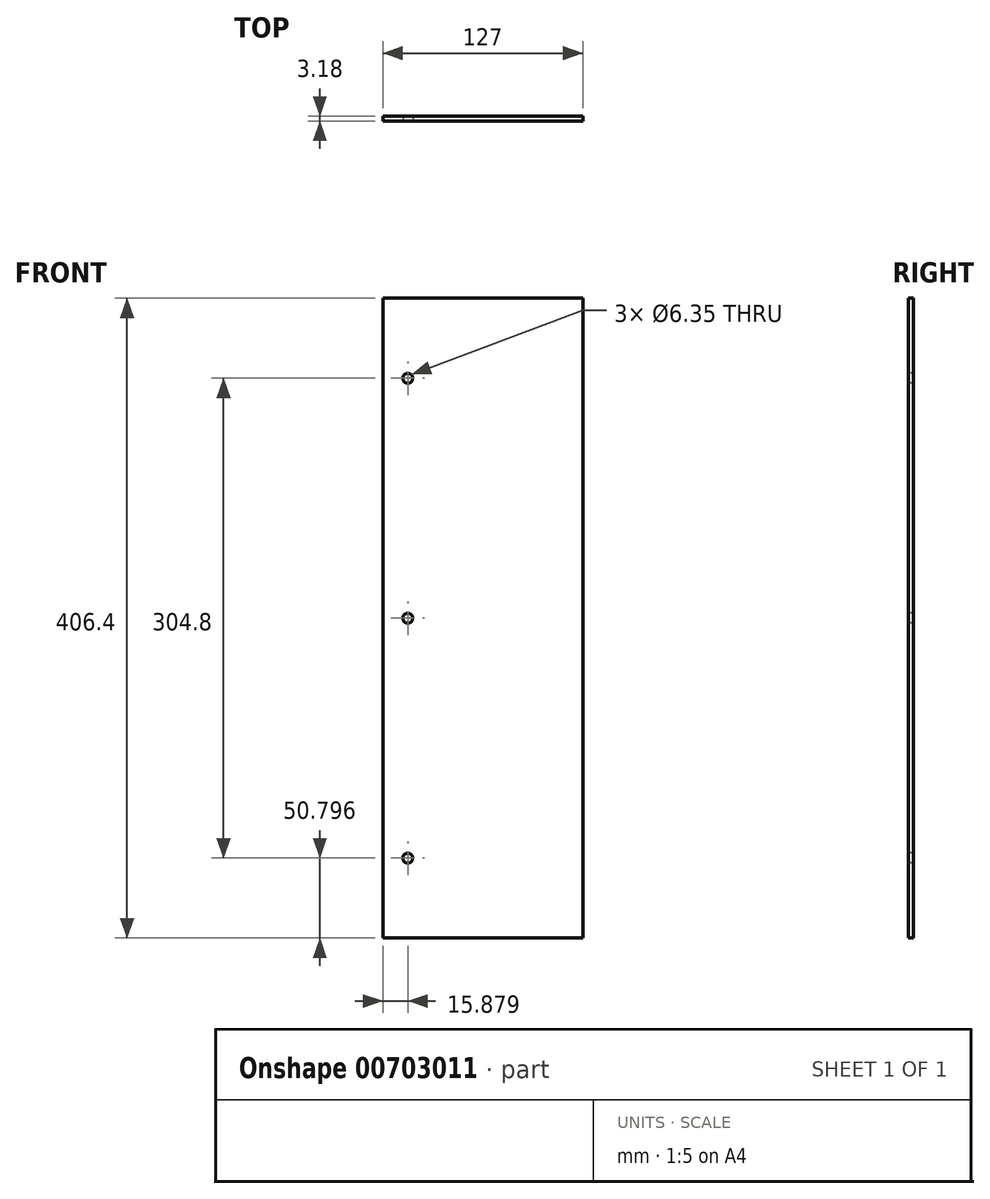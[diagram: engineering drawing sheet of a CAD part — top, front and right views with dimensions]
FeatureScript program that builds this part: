
annotation { "Feature Type Name" : "Feature", "Feature Type Description" : "" }
export const myFeature = defineFeature(function(context is Context, id is Id, definition is map)
    precondition{}
    {
        {
            var Q0;
            Q0=qCreatedBy(makeId("Front.planeOp"),FACE);
            var sketch = newSketch(context, id + "F0", { "sketchPlane" : qUnion([Q0])});
            skLineSegment(sketch, "E0.bottom", {"start": v(-66.76, 437.09) * mm, "end": v(60.24, 437.09) * mm});
            skLineSegment(sketch, "E0.top", {"start": v(-66.76, 30.69) * mm, "end": v(60.24, 30.69) * mm});
            skLineSegment(sketch, "E0.left", {"start": v(-66.76, 437.09) * mm, "end": v(-66.76, 30.69) * mm});
            skLineSegment(sketch, "E0.right", {"start": v(60.24, 437.09) * mm, "end": v(60.24, 30.69) * mm});
            skSolve(sketch);
        }
        {
            var Q0;
            Q0=makeQuery(id+"F0.imprint","IMPRINT",FACE,{"disambiguationData":[TD([[makeQuery(id+"F0.imprint","IMPRINT",EDGE,{"derivedFrom":sQuery(id+"F0.wireOp",EDGE,"E0.bottom")}),-1.0]])]});
            extrude(context, id + "F1", {"entities" : qUnion([Q0]), "depth" : 3.17 * mm, "offsetDistance" : 25.4 * mm});
        }
        {
            var Q0;
            Q0=makeQuery(id+"F1.opExtrude","CAP_FACE",FACE,{"disambiguationData":[OSD([sQuery(id+"F0.wireOp",EDGE,"E0.bottom"),sQuery(id+"F0.wireOp",EDGE,"E0.top"),sQuery(id+"F0.wireOp",EDGE,"E0.left"),sQuery(id+"F0.wireOp",EDGE,"E0.right")])],"isStart":false});
            var sketch = newSketch(context, id + "F2", { "sketchPlane" : qUnion([Q0])});
            skLineSegment(sketch, "E1", {"start": v(-66.76, 437.09) * mm, "end": v(-50.88, 437.09) * mm});
            skLineSegment(sketch, "E2", {"start": v(-50.88, 437.09) * mm, "end": v(-50.88, 30.69) * mm});
            skLineSegment(sketch, "E3", {"start": v(-50.88, 30.69) * mm, "end": v(-50.88, 81.49) * mm});
            skLineSegment(sketch, "E4", {"start": v(-50.88, 437.09) * mm, "end": v(-50.88, 386.29) * mm});
            skPoint(sketch, "E5", {"position": v(-50.88, 386.29) * mm});
            skPoint(sketch, "E6", {"position": v(-50.88, 233.89) * mm});
            skPoint(sketch, "E7", {"position": v(-50.88, 81.49) * mm});
            skSolve(sketch);
        }
        {
            var Q0;
            Q0=sQuery(id+"F2.wireOp",VERTEX,"E7");
            var Q1;
            Q1=sQuery(id+"F2.wireOp",VERTEX,"E6");
            var Q2;
            Q2=sQuery(id+"F2.wireOp",VERTEX,"E5");
            var Q3;
            Q3=makeQuery(id+"F1.opExtrude","SWEPT_BODY",BODY,{"disambiguationData":[OSD([sQuery(id+"F0.wireOp",EDGE,"E0.bottom"),sQuery(id+"F0.wireOp",EDGE,"E0.top"),sQuery(id+"F0.wireOp",EDGE,"E0.left"),sQuery(id+"F0.wireOp",EDGE,"E0.right")])]});
            hole(context, id + "F3", {"style" : HoleStyle.SIMPLE, "endStyle" : HoleEndStyle.THROUGH, "holeDiameter" : 6.35 * mm, "majorDiameter" : 6.35 * mm, "isTappedThrough" : true, "tappedDepth" : 12.7 * mm, "tapClearance" : 3, "locations" : qUnion([Q0, Q1, Q2]), "scope" : qUnion([Q3])});
        }
    });
